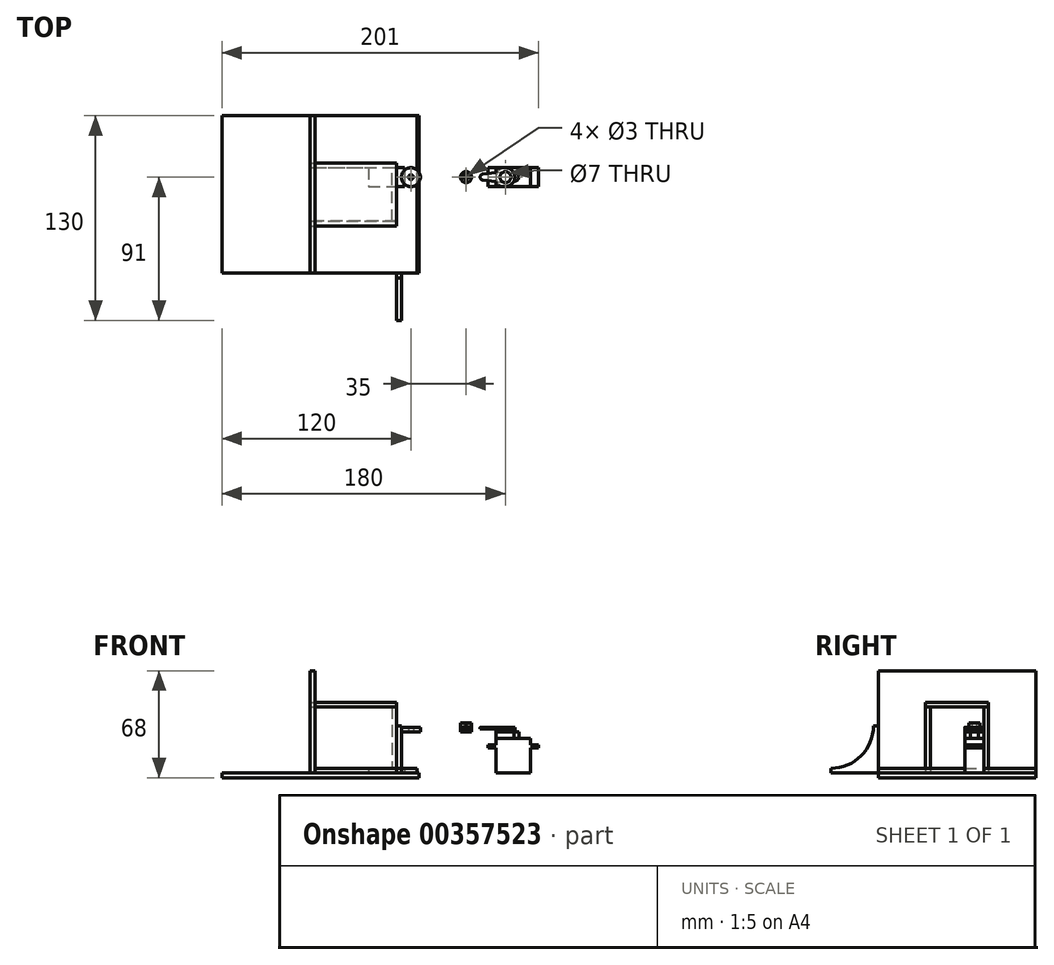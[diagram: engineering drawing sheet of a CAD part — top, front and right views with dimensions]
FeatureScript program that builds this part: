
annotation { "Feature Type Name" : "Feature", "Feature Type Description" : "" }
export const myFeature = defineFeature(function(context is Context, id is Id, definition is map)
    precondition{}
    {
        {
            var Q0;
            Q0=qCreatedBy(makeId("Front.planeOp"),FACE);
            var sketch = newSketch(context, id + "F0", { "sketchPlane" : qUnion([Q0])});
            skLineSegment(sketch, "E0", {"start": v(0, 0) * mm, "end": v(22, 0) * mm});
            skLineSegment(sketch, "E1", {"start": v(22, 0) * mm, "end": v(22, 16) * mm});
            skLineSegment(sketch, "E2", {"start": v(22, 16) * mm, "end": v(27, 16) * mm});
            skLineSegment(sketch, "E3", {"start": v(27, 16) * mm, "end": v(27, 18) * mm});
            skLineSegment(sketch, "E4", {"start": v(27, 18) * mm, "end": v(22, 18) * mm});
            skLineSegment(sketch, "E5", {"start": v(22, 18) * mm, "end": v(22, 22) * mm});
            skLineSegment(sketch, "E6", {"start": v(22, 22) * mm, "end": v(0, 22) * mm});
            skLineSegment(sketch, "E7", {"start": v(0, 22) * mm, "end": v(0, 18) * mm});
            skLineSegment(sketch, "E8", {"start": v(0, 18) * mm, "end": v(-5, 18) * mm});
            skLineSegment(sketch, "E9", {"start": v(-5, 18) * mm, "end": v(-5, 16) * mm});
            skLineSegment(sketch, "E10", {"start": v(-5, 16) * mm, "end": v(0, 16) * mm});
            skLineSegment(sketch, "E11", {"start": v(0, 16) * mm, "end": v(0, 0) * mm});
            skSolve(sketch);
        }
        {
            var Q0;
            Q0=makeQuery(id+"F0.imprint","IMPRINT",FACE,{"disambiguationData":[TD([[makeQuery(id+"F0.imprint","IMPRINT",EDGE,{"derivedFrom":sQuery(id+"F0.wireOp",EDGE,"E0")}),1.0]])]});
            extrude(context, id + "F1", {"entities" : qUnion([Q0]), "oppositeDirection" : true, "depth" : 17 * mm, "hasSecondDirection" : true, "secondDirectionOppositeDirection" : true, "secondDirectionDepth" : 5 * mm});
        }
        {
            var Q0;
            Q0=qCreatedBy(makeId("Right.planeOp"),FACE);
            cPlane(context, id + "F2", {"entities" : qUnion([Q0]), "cplaneType" : CPlaneType.OFFSET, "offset" : 63 * mm, "oppositeDirection" : true, "width" : 150 * mm, "height" : 150 * mm});
        }
        {
            var Q0;
            Q0=makeQuery(id+"F1.opExtrude","SWEPT_FACE",FACE,{"disambiguationData":[OSD([sQuery(id+"F0.wireOp",EDGE,"E6")])]});
            var sketch = newSketch(context, id + "F3", { "sketchPlane" : qUnion([Q0])});
            skCircle(sketch, "E12", {"center": v(6, 11) * mm, "radius": 6 * mm});
            skCircle(sketch, "E13", {"center": v(12, 11) * mm, "radius": 2.5 * mm});
            skCircle(sketch, "E14", {"center": v(-19, 11) * mm, "radius": 3.5 * mm});
            skLineSegment(sketch, "E15", {"start": v(-19.35, 7.52) * mm, "end": v(5.4, 5.03) * mm});
            skLineSegment(sketch, "E16", {"start": v(-19.35, 14.48) * mm, "end": v(5.4, 16.97) * mm});
            skCircle(sketch, "E17", {"center": v(-54, 11) * mm, "radius": 6 * mm});
            skLineSegment(sketch, "E18", {"start": v(-54, 5) * mm, "end": v(-63, 5) * mm});
            skLineSegment(sketch, "E19", {"start": v(-63, 17) * mm, "end": v(-54, 17) * mm});
            skLineSegment(sketch, "E20", {"start": v(6, 11) * mm, "end": v(12, 11) * mm, "construction": true});
            skLineSegment(sketch, "E21", {"start": v(6, 11) * mm, "end": v(-19, 11) * mm, "construction": true});
            skLineSegment(sketch, "E22", {"start": v(-19, 11) * mm, "end": v(-54, 11) * mm, "construction": true});
            skLineSegment(sketch, "E23", {"start": v(-53.57, 16.98) * mm, "end": v(-18.75, 14.5) * mm});
            skLineSegment(sketch, "E24", {"start": v(-53.57, 5.02) * mm, "end": v(-18.75, 7.5) * mm});
            skCircle(sketch, "E25", {"center": v(-54, 11) * mm, "radius": 1.5 * mm});
            skCircle(sketch, "E26", {"center": v(-19, 11) * mm, "radius": 1.5 * mm});
            skCircle(sketch, "E27", {"center": v(6, 11) * mm, "radius": 3.5 * mm});
            skCircle(sketch, "E28", {"center": v(-8, 11) * mm, "radius": 2 * mm});
            skLineSegment(sketch, "E29", {"start": v(-8.21, 9.01) * mm, "end": v(5.62, 7.52) * mm});
            skLineSegment(sketch, "E30", {"start": v(-8.21, 12.99) * mm, "end": v(5.63, 14.48) * mm});
            skLineSegment(sketch, "E31", {"start": v(-63, 17) * mm, "end": v(-63, 14) * mm});
            skLineSegment(sketch, "E32", {"start": v(-63, 14) * mm, "end": v(-66, 14) * mm});
            skLineSegment(sketch, "E33", {"start": v(-66, 14) * mm, "end": v(-66, 8) * mm});
            skLineSegment(sketch, "E34", {"start": v(-66, 8) * mm, "end": v(-63, 8) * mm});
            skLineSegment(sketch, "E35", {"start": v(-63, 8) * mm, "end": v(-63, 5) * mm});
            skSolve(sketch);
        }
        {
            var Q0;
            {var subQ0=sQuery(id+"F3.wireOp",EDGE,"E12");var subQ1=sQuery(id+"F0.wireOp",EDGE,"E6");var subQ3=makeQuery(id+"F3.imprint","INTERSECT",VERTEX,{"derivedFrom":[makeQuery(id+"F1.opExtrude","CAP_EDGE",EDGE,{"disambiguationData":[OSD([subQ1])],"isStart":true}),subQ0]});Q0=makeQuery(id+"F3.imprint","IMPRINT",FACE,{"disambiguationData":[TD([[makeQuery(id+"F3.imprint","IMPRINT",EDGE,{"disambiguationData":[TD([[subQ3,1.0]])],"derivedFrom":subQ0}),1.0]])]});}
            var Q1;
            {var subQ0=sQuery(id+"F3.wireOp",EDGE,"E13");var subQ1=sQuery(id+"F3.wireOp",EDGE,"E12");var subQ2=makeQuery(id+"F3.imprint","INTERSECT",VERTEX,{"disambiguationData":[OD(0.0)],"derivedFrom":[subQ1,subQ0]});Q1=makeQuery(id+"F3.imprint","IMPRINT",FACE,{"disambiguationData":[TD([[makeQuery(id+"F3.imprint","IMPRINT",EDGE,{"disambiguationData":[TD([[subQ2,1.0]])],"derivedFrom":subQ1}),1.0]])]});}
            var Q2;
            {var subQ0=sQuery(id+"F3.wireOp",EDGE,"E13");var subQ1=sQuery(id+"F3.wireOp",EDGE,"E12");var subQ2=makeQuery(id+"F3.imprint","INTERSECT",VERTEX,{"disambiguationData":[OD(0.0)],"derivedFrom":[subQ1,subQ0]});Q2=makeQuery(id+"F3.imprint","IMPRINT",FACE,{"disambiguationData":[TD([[makeQuery(id+"F3.imprint","IMPRINT",EDGE,{"disambiguationData":[TD([[subQ2,1.0]])],"derivedFrom":subQ1}),-1.0]])]});}
            var Q3;
            {var subQ0=sQuery(id+"F3.wireOp",EDGE,"E13");var subQ1=sQuery(id+"F3.wireOp",EDGE,"E12");var subQ2=makeQuery(id+"F3.imprint","INTERSECT",VERTEX,{"disambiguationData":[OD(0.0)],"derivedFrom":[subQ1,subQ0]});Q3=makeQuery(id+"F3.imprint","IMPRINT",FACE,{"disambiguationData":[TD([[makeQuery(id+"F3.imprint","IMPRINT",EDGE,{"disambiguationData":[TD([[subQ2,-1.0]])],"derivedFrom":subQ1}),1.0]])]});}
            var Q4;
            {var subQ0=sQuery(id+"F3.wireOp",EDGE,"E29");var subQ1=sQuery(id+"F3.wireOp",EDGE,"E27");var subQ2=makeQuery(id+"F3.imprint","INTERSECT",VERTEX,{"derivedFrom":[subQ1,subQ0]});Q4=makeQuery(id+"F3.imprint","IMPRINT",FACE,{"disambiguationData":[TD([[makeQuery(id+"F3.imprint","IMPRINT",EDGE,{"disambiguationData":[TD([[subQ2,1.0]])],"derivedFrom":subQ1}),-1.0]])]});}
            var Q5;
            {var subQ0=sQuery(id+"F3.wireOp",EDGE,"E27");var subQ1=makeQuery(id+"F3.imprint","INTERSECT",VERTEX,{"derivedFrom":[subQ0,sQuery(id+"F3.wireOp",EDGE,"E30")]});Q5=makeQuery(id+"F3.imprint","IMPRINT",FACE,{"disambiguationData":[TD([[makeQuery(id+"F3.imprint","IMPRINT",EDGE,{"disambiguationData":[TD([[subQ1,1.0]])],"derivedFrom":subQ0}),1.0]])]});}
            extrude(context, id + "F4", {"entities" : qUnion([Q0, Q1, Q2, Q3, Q4, Q5]), "operationType" : NewBodyOperationType.ADD, "depth" : 4 * mm});
        }
        {
            var Q0;
            {var subQ0=sQuery(id+"F3.wireOp",EDGE,"E15");var subQ1=sQuery(id+"F3.wireOp",EDGE,"E12");var subQ2=makeQuery(id+"F3.imprint","INTERSECT",VERTEX,{"derivedFrom":[subQ1,subQ0]});Q0=makeQuery(id+"F3.imprint","IMPRINT",FACE,{"disambiguationData":[TD([[makeQuery(id+"F3.imprint","IMPRINT",EDGE,{"disambiguationData":[TD([[subQ2,1.0]])],"derivedFrom":subQ1}),-1.0]])]});}
            var Q1;
            Q1=makeQuery(id+"F3.imprint","IMPRINT",FACE,{"disambiguationData":[TD([[makeQuery(id+"F3.imprint","IMPRINT",EDGE,{"derivedFrom":sQuery(id+"F3.wireOp",EDGE,"E26")}),-1.0]])]});
            var Q2;
            {var subQ0=sQuery(id+"F3.wireOp",EDGE,"E13");var subQ1=sQuery(id+"F3.wireOp",EDGE,"E12");var subQ2=makeQuery(id+"F3.imprint","INTERSECT",VERTEX,{"disambiguationData":[OD(0.0)],"derivedFrom":[subQ1,subQ0]});Q2=makeQuery(id+"F3.imprint","IMPRINT",FACE,{"disambiguationData":[TD([[makeQuery(id+"F3.imprint","IMPRINT",EDGE,{"disambiguationData":[TD([[subQ2,-1.0]])],"derivedFrom":subQ1}),1.0]])]});}
            var Q3;
            {var subQ0=sQuery(id+"F3.wireOp",EDGE,"E13");var subQ1=sQuery(id+"F3.wireOp",EDGE,"E12");var subQ2=makeQuery(id+"F3.imprint","INTERSECT",VERTEX,{"disambiguationData":[OD(0.0)],"derivedFrom":[subQ1,subQ0]});Q3=makeQuery(id+"F3.imprint","IMPRINT",FACE,{"disambiguationData":[TD([[makeQuery(id+"F3.imprint","IMPRINT",EDGE,{"disambiguationData":[TD([[subQ2,1.0]])],"derivedFrom":subQ1}),1.0]])]});}
            var Q4;
            {var subQ0=sQuery(id+"F3.wireOp",EDGE,"E16");var subQ1=sQuery(id+"F3.wireOp",EDGE,"E12");var subQ2=makeQuery(id+"F3.imprint","INTERSECT",VERTEX,{"derivedFrom":[subQ1,subQ0]});Q4=makeQuery(id+"F3.imprint","IMPRINT",FACE,{"disambiguationData":[TD([[makeQuery(id+"F3.imprint","IMPRINT",EDGE,{"disambiguationData":[TD([[subQ2,-1.0]])],"derivedFrom":subQ1}),-1.0]])]});}
            var Q5;
            {var subQ5=sQuery(id+"F3.wireOp",EDGE,"E23");var subQ6=sQuery(id+"F3.wireOp",EDGE,"E14");var subQ7=makeQuery(id+"F3.imprint","INTERSECT",VERTEX,{"derivedFrom":[subQ6,subQ5]});Q5=makeQuery(id+"F3.imprint","IMPRINT",FACE,{"disambiguationData":[TD([[makeQuery(id+"F3.imprint","IMPRINT",EDGE,{"disambiguationData":[TD([[subQ7,-1.0]])],"derivedFrom":subQ6}),1.0]])]});}
            var Q6;
            {var subQ1=sQuery(id+"F3.wireOp",EDGE,"E12");var subQ4=makeQuery(id+"F3.imprint","INTERSECT",VERTEX,{"derivedFrom":[subQ1,sQuery(id+"F3.wireOp",EDGE,"E15")]});Q6=makeQuery(id+"F3.imprint","IMPRINT",FACE,{"disambiguationData":[TD([[makeQuery(id+"F3.imprint","IMPRINT",EDGE,{"disambiguationData":[TD([[subQ4,1.0]])],"derivedFrom":subQ1}),1.0]])]});}
            var Q7;
            {var subQ0=sQuery(id+"F3.wireOp",EDGE,"E16");var subQ1=sQuery(id+"F3.wireOp",EDGE,"E14");var subQ2=makeQuery(id+"F3.imprint","INTERSECT",VERTEX,{"derivedFrom":[subQ1,subQ0]});Q7=makeQuery(id+"F3.imprint","IMPRINT",FACE,{"disambiguationData":[TD([[makeQuery(id+"F3.imprint","IMPRINT",EDGE,{"disambiguationData":[TD([[subQ2,-1.0]])],"derivedFrom":subQ1}),1.0]])]});}
            var Q8;
            {var subQ0=sQuery(id+"F3.wireOp",EDGE,"E15");var subQ1=sQuery(id+"F3.wireOp",EDGE,"E14");var subQ2=makeQuery(id+"F3.imprint","INTERSECT",VERTEX,{"derivedFrom":[subQ1,subQ0]});Q8=makeQuery(id+"F3.imprint","IMPRINT",FACE,{"disambiguationData":[TD([[makeQuery(id+"F3.imprint","IMPRINT",EDGE,{"disambiguationData":[TD([[subQ2,1.0]])],"derivedFrom":subQ1}),1.0]])]});}
            extrude(context, id + "F5", {"entities" : qUnion([Q0, Q1, Q2, Q3, Q4, Q5, Q6, Q7, Q8]), "depth" : 6 * mm, "hasSecondDirection" : true, "secondDirectionOppositeDirection" : false, "secondDirectionDepth" : 4 * mm});
        }
        {
            var Q0;
            Q0=makeQuery(id+"F3.imprint","IMPRINT",FACE,{"disambiguationData":[TD([[makeQuery(id+"F3.imprint","IMPRINT",EDGE,{"derivedFrom":sQuery(id+"F3.wireOp",EDGE,"E26")}),-1.0]])]});
            var Q1;
            {var subQ5=sQuery(id+"F3.wireOp",EDGE,"E23");var subQ6=sQuery(id+"F3.wireOp",EDGE,"E14");var subQ7=makeQuery(id+"F3.imprint","INTERSECT",VERTEX,{"derivedFrom":[subQ6,subQ5]});Q1=makeQuery(id+"F3.imprint","IMPRINT",FACE,{"disambiguationData":[TD([[makeQuery(id+"F3.imprint","IMPRINT",EDGE,{"disambiguationData":[TD([[subQ7,-1.0]])],"derivedFrom":subQ6}),1.0]])]});}
            var Q2;
            {var subQ0=sQuery(id+"F3.wireOp",EDGE,"E28");var subQ1=makeQuery(id+"F3.imprint","INTERSECT",VERTEX,{"derivedFrom":[subQ0,sQuery(id+"F3.wireOp",EDGE,"E29")]});Q2=makeQuery(id+"F3.imprint","IMPRINT",FACE,{"disambiguationData":[TD([[makeQuery(id+"F3.imprint","IMPRINT",EDGE,{"disambiguationData":[TD([[subQ1,1.0]])],"derivedFrom":subQ0}),1.0]])]});}
            var Q3;
            {var subQ1=sQuery(id+"F3.wireOp",EDGE,"E28");var subQ6=sQuery(id+"F3.wireOp",EDGE,"E29");var subQ8=makeQuery(id+"F3.imprint","INTERSECT",VERTEX,{"derivedFrom":[subQ1,subQ6]});Q3=makeQuery(id+"F3.imprint","IMPRINT",FACE,{"disambiguationData":[TD([[makeQuery(id+"F3.imprint","IMPRINT",EDGE,{"disambiguationData":[TD([[subQ8,-1.0]])],"derivedFrom":subQ1}),-1.0]])]});}
            var Q4;
            {var subQ0=sQuery(id+"F3.wireOp",EDGE,"E16");var subQ1=sQuery(id+"F3.wireOp",EDGE,"E12");var subQ2=makeQuery(id+"F3.imprint","INTERSECT",VERTEX,{"derivedFrom":[subQ1,subQ0]});Q4=makeQuery(id+"F3.imprint","IMPRINT",FACE,{"disambiguationData":[TD([[makeQuery(id+"F3.imprint","IMPRINT",EDGE,{"disambiguationData":[TD([[subQ2,-1.0]])],"derivedFrom":subQ1}),-1.0]])]});}
            var Q5;
            {var subQ0=sQuery(id+"F3.wireOp",EDGE,"E30");var subQ1=sQuery(id+"F3.wireOp",EDGE,"E12");var subQ2=makeQuery(id+"F3.imprint","INTERSECT",VERTEX,{"derivedFrom":[subQ1,subQ0]});Q5=makeQuery(id+"F3.imprint","IMPRINT",FACE,{"disambiguationData":[TD([[makeQuery(id+"F3.imprint","IMPRINT",EDGE,{"disambiguationData":[TD([[subQ2,-1.0]])],"derivedFrom":subQ1}),-1.0]])]});}
            var Q6;
            {var subQ0=sQuery(id+"F3.wireOp",EDGE,"E29");var subQ1=sQuery(id+"F3.wireOp",EDGE,"E12");var subQ2=makeQuery(id+"F3.imprint","INTERSECT",VERTEX,{"derivedFrom":[subQ1,subQ0]});Q6=makeQuery(id+"F3.imprint","IMPRINT",FACE,{"disambiguationData":[TD([[makeQuery(id+"F3.imprint","IMPRINT",EDGE,{"disambiguationData":[TD([[subQ2,1.0]])],"derivedFrom":subQ1}),-1.0]])]});}
            var Q7;
            {var subQ0=sQuery(id+"F3.wireOp",EDGE,"E15");var subQ1=sQuery(id+"F3.wireOp",EDGE,"E12");var subQ2=makeQuery(id+"F3.imprint","INTERSECT",VERTEX,{"derivedFrom":[subQ1,subQ0]});Q7=makeQuery(id+"F3.imprint","IMPRINT",FACE,{"disambiguationData":[TD([[makeQuery(id+"F3.imprint","IMPRINT",EDGE,{"disambiguationData":[TD([[subQ2,1.0]])],"derivedFrom":subQ1}),-1.0]])]});}
            var Q8;
            {var subQ0=sQuery(id+"F3.wireOp",EDGE,"E29");var subQ1=sQuery(id+"F3.wireOp",EDGE,"E27");var subQ2=makeQuery(id+"F3.imprint","INTERSECT",VERTEX,{"derivedFrom":[subQ1,subQ0]});Q8=makeQuery(id+"F3.imprint","IMPRINT",FACE,{"disambiguationData":[TD([[makeQuery(id+"F3.imprint","IMPRINT",EDGE,{"disambiguationData":[TD([[subQ2,1.0]])],"derivedFrom":subQ1}),-1.0]])]});}
            var Q9;
            {var subQ0=sQuery(id+"F3.wireOp",EDGE,"E13");var subQ1=sQuery(id+"F3.wireOp",EDGE,"E12");var subQ2=makeQuery(id+"F3.imprint","INTERSECT",VERTEX,{"disambiguationData":[OD(0.0)],"derivedFrom":[subQ1,subQ0]});Q9=makeQuery(id+"F3.imprint","IMPRINT",FACE,{"disambiguationData":[TD([[makeQuery(id+"F3.imprint","IMPRINT",EDGE,{"disambiguationData":[TD([[subQ2,-1.0]])],"derivedFrom":subQ1}),1.0]])]});}
            var Q10;
            {var subQ1=sQuery(id+"F3.wireOp",EDGE,"E12");var subQ4=makeQuery(id+"F3.imprint","INTERSECT",VERTEX,{"derivedFrom":[subQ1,sQuery(id+"F3.wireOp",EDGE,"E15")]});Q10=makeQuery(id+"F3.imprint","IMPRINT",FACE,{"disambiguationData":[TD([[makeQuery(id+"F3.imprint","IMPRINT",EDGE,{"disambiguationData":[TD([[subQ4,1.0]])],"derivedFrom":subQ1}),1.0]])]});}
            var Q11;
            {var subQ0=sQuery(id+"F3.wireOp",EDGE,"E13");var subQ1=sQuery(id+"F3.wireOp",EDGE,"E12");var subQ2=makeQuery(id+"F3.imprint","INTERSECT",VERTEX,{"disambiguationData":[OD(0.0)],"derivedFrom":[subQ1,subQ0]});Q11=makeQuery(id+"F3.imprint","IMPRINT",FACE,{"disambiguationData":[TD([[makeQuery(id+"F3.imprint","IMPRINT",EDGE,{"disambiguationData":[TD([[subQ2,1.0]])],"derivedFrom":subQ1}),1.0]])]});}
            var Q12;
            {var subQ0=sQuery(id+"F3.wireOp",EDGE,"E15");var subQ1=sQuery(id+"F3.wireOp",EDGE,"E14");var subQ2=makeQuery(id+"F3.imprint","INTERSECT",VERTEX,{"derivedFrom":[subQ1,subQ0]});Q12=makeQuery(id+"F3.imprint","IMPRINT",FACE,{"disambiguationData":[TD([[makeQuery(id+"F3.imprint","IMPRINT",EDGE,{"disambiguationData":[TD([[subQ2,1.0]])],"derivedFrom":subQ1}),1.0]])]});}
            var Q13;
            {var subQ0=sQuery(id+"F3.wireOp",EDGE,"E16");var subQ1=sQuery(id+"F3.wireOp",EDGE,"E14");var subQ2=makeQuery(id+"F3.imprint","INTERSECT",VERTEX,{"derivedFrom":[subQ1,subQ0]});Q13=makeQuery(id+"F3.imprint","IMPRINT",FACE,{"disambiguationData":[TD([[makeQuery(id+"F3.imprint","IMPRINT",EDGE,{"disambiguationData":[TD([[subQ2,-1.0]])],"derivedFrom":subQ1}),1.0]])]});}
            extrude(context, id + "F6", {"entities" : qUnion([Q0, Q1, Q2, Q3, Q4, Q5, Q6, Q7, Q8, Q9, Q10, Q11, Q12, Q13]), "depth" : 7 * mm, "hasSecondDirection" : true, "secondDirectionOppositeDirection" : false, "secondDirectionDepth" : 6 * mm});
        }
        {
            var Q0;
            {var subQ0=sQuery(id+"F3.wireOp",EDGE,"E14");var subQ1=makeQuery(id+"F3.imprint","INTERSECT",VERTEX,{"derivedFrom":[subQ0,sQuery(id+"F3.wireOp",EDGE,"E15"),sQuery(id+"F3.wireOp",EDGE,"TpgKvrXl-maDU-2S3D-b7ML-qU1TAJrhzgWD")]});Q0=makeQuery(id+"F3.imprint","IMPRINT",FACE,{"disambiguationData":[TD([[makeQuery(id+"F3.imprint","IMPRINT",EDGE,{"disambiguationData":[TD([[subQ1,-1.0]])],"derivedFrom":subQ0}),1.0]])]});}
            var Q1;
            {var subQ0=sQuery(id+"F3.wireOp",EDGE,"E17");var subQ1=makeQuery(id+"F3.imprint","INTERSECT",VERTEX,{"derivedFrom":[sQuery(id+"F3.wireOp",EDGE,"TpgKvrXl-maDU-2S3D-b7ML-qU1TAJrhzgWD"),subQ0,sQuery(id+"F3.wireOp",EDGE,"E18")]});Q1=makeQuery(id+"F3.imprint","IMPRINT",FACE,{"disambiguationData":[TD([[makeQuery(id+"F3.imprint","IMPRINT",EDGE,{"disambiguationData":[TD([[subQ1,-1.0]])],"derivedFrom":subQ0}),-1.0]])]});}
            var Q2;
            {var subQ0=sQuery(id+"F3.wireOp",EDGE,"E14");var subQ1=makeQuery(id+"F3.imprint","INTERSECT",VERTEX,{"derivedFrom":[subQ0,sQuery(id+"F3.wireOp",EDGE,"E15"),sQuery(id+"F3.wireOp",EDGE,"TpgKvrXl-maDU-2S3D-b7ML-qU1TAJrhzgWD")]});Q2=makeQuery(id+"F3.imprint","IMPRINT",FACE,{"disambiguationData":[TD([[makeQuery(id+"F3.imprint","IMPRINT",EDGE,{"disambiguationData":[TD([[subQ1,-1.0]])],"derivedFrom":subQ0}),-1.0]])]});}
            var Q3;
            {var subQ0=sQuery(id+"F3.wireOp",EDGE,"E15");var subQ1=sQuery(id+"F3.wireOp",EDGE,"E14");var subQ2=makeQuery(id+"F3.imprint","INTERSECT",VERTEX,{"derivedFrom":[subQ1,subQ0]});Q3=makeQuery(id+"F3.imprint","IMPRINT",FACE,{"disambiguationData":[TD([[makeQuery(id+"F3.imprint","IMPRINT",EDGE,{"disambiguationData":[TD([[subQ2,1.0]])],"derivedFrom":subQ1}),1.0]])]});}
            var Q4;
            {var subQ0=sQuery(id+"F3.wireOp",EDGE,"E16");var subQ1=sQuery(id+"F3.wireOp",EDGE,"E14");var subQ2=makeQuery(id+"F3.imprint","INTERSECT",VERTEX,{"derivedFrom":[subQ1,subQ0]});Q4=makeQuery(id+"F3.imprint","IMPRINT",FACE,{"disambiguationData":[TD([[makeQuery(id+"F3.imprint","IMPRINT",EDGE,{"disambiguationData":[TD([[subQ2,-1.0]])],"derivedFrom":subQ1}),1.0]])]});}
            extrude(context, id + "F7", {"entities" : qUnion([Q0, Q1, Q2, Q3, Q4]), "depth" : 10 * mm, "hasSecondDirection" : true, "secondDirectionOppositeDirection" : false, "secondDirectionDepth" : 7 * mm});
        }
        {
            var Q0;
            Q0=qCreatedBy(id+"F2.planeOp",FACE);
            var sketch = newSketch(context, id + "F8", { "sketchPlane" : qUnion([Q0])});
            skLineSegment(sketch, "E36.bottom", {"start": v(-20, 0) * mm, "end": v(20, 0) * mm});
            skLineSegment(sketch, "E36.top", {"start": v(-20, 45) * mm, "end": v(20, 45) * mm});
            skLineSegment(sketch, "E36.left", {"start": v(-20, 0) * mm, "end": v(-20, 45) * mm});
            skLineSegment(sketch, "E36.right", {"start": v(20, 0) * mm, "end": v(20, 45) * mm});
            skLineSegment(sketch, "E37", {"start": v(-20, 42) * mm, "end": v(20, 42) * mm});
            skLineSegment(sketch, "E38", {"start": v(-17, 42) * mm, "end": v(-17, 0) * mm});
            skLineSegment(sketch, "E39", {"start": v(17, 42) * mm, "end": v(17, 0) * mm});
            skLineSegment(sketch, "E40", {"start": v(-20, 0) * mm, "end": v(-50, 0) * mm});
            skLineSegment(sketch, "E41", {"start": v(-50, 0) * mm, "end": v(-50, 65) * mm});
            skLineSegment(sketch, "E42", {"start": v(-50, 65) * mm, "end": v(50, 65) * mm});
            skLineSegment(sketch, "E43", {"start": v(50, 65) * mm, "end": v(50, 0) * mm});
            skLineSegment(sketch, "E44", {"start": v(50, 0) * mm, "end": v(20, 0) * mm});
            skLineSegment(sketch, "E45", {"start": v(-50, 0) * mm, "end": v(-50, -3) * mm});
            skLineSegment(sketch, "E46", {"start": v(-50, -3) * mm, "end": v(50, -3) * mm});
            skLineSegment(sketch, "E47", {"start": v(50, -3) * mm, "end": v(50, 0) * mm});
            skLineSegment(sketch, "E48", {"start": v(-17, 3) * mm, "end": v(17, 3) * mm});
            skLineSegment(sketch, "E49", {"start": v(-50, 0) * mm, "end": v(-80, 0) * mm});
            skLineSegment(sketch, "E50", {"start": v(-80, 0) * mm, "end": v(-80, 3) * mm});
            skLineSegment(sketch, "E51", {"start": v(-53, 30) * mm, "end": v(-50, 30) * mm});
            skLineSegment(sketch, "E52", {"start": v(-50, 30) * mm, "end": v(-50, 0) * mm});
            skArc(sketch, "E53", {"start": v(-80, 3) * mm, "mid": v(-60.9, 10.9) * mm, "end": v(-53, 30) * mm});
            skSolve(sketch);
        }
        {
            var Q0;
            {var subQ3=sQuery(id+"F8.wireOp",EDGE,"E38");Q0=makeQuery(id+"F8.imprint","IMPRINT",FACE,{"disambiguationData":[TD([[makeQuery(id+"F8.imprint","IMPRINT",EDGE,{"derivedFrom":subQ3}),-1.0]])]});}
            extrude(context, id + "F9", {"entities" : qUnion([Q0]), "oppositeDirection" : true, "depth" : 55 * mm});
        }
        {
            var Q0;
            {var subQ3=sQuery(id+"F8.wireOp",EDGE,"E39");Q0=makeQuery(id+"F8.imprint","IMPRINT",FACE,{"disambiguationData":[TD([[makeQuery(id+"F8.imprint","IMPRINT",EDGE,{"derivedFrom":subQ3}),1.0]])]});}
            extrude(context, id + "F10", {"entities" : qUnion([Q0]), "oppositeDirection" : true, "depth" : 55 * mm});
        }
        {
            var Q0;
            {var subQ1=sQuery(id+"F8.wireOp",EDGE,"E36.top");Q0=makeQuery(id+"F8.imprint","IMPRINT",FACE,{"disambiguationData":[TD([[makeQuery(id+"F8.imprint","IMPRINT",EDGE,{"derivedFrom":subQ1}),-1.0]])]});}
            extrude(context, id + "F11", {"entities" : qUnion([Q0]), "oppositeDirection" : true, "depth" : 55 * mm});
        }
        {
            var Q0;
            {var subQ5=sQuery(id+"F8.wireOp",EDGE,"E48");Q0=makeQuery(id+"F8.imprint","IMPRINT",FACE,{"disambiguationData":[TD([[makeQuery(id+"F8.imprint","IMPRINT",EDGE,{"derivedFrom":subQ5}),1.0]])]});}
            extrude(context, id + "F12", {"entities" : qUnion([Q0]), "oppositeDirection" : true, "depth" : 3 * mm});
        }
        {
            var Q0;
            {var subQ0=sQuery(id+"F8.wireOp",EDGE,"E38");Q0=makeQuery(id+"F8.imprint","IMPRINT",FACE,{"disambiguationData":[TD([[makeQuery(id+"F8.imprint","IMPRINT",EDGE,{"derivedFrom":subQ0}),1.0]])]});}
            extrude(context, id + "F13", {"entities" : qUnion([Q0]), "oppositeDirection" : true, "depth" : 55 * mm, "hasSecondDirection" : true, "secondDirectionOppositeDirection" : true, "secondDirectionDepth" : 52 * mm});
        }
        {
            var Q0;
            {var subQ0=sQuery(id+"F3.wireOp",EDGE,"E17");var subQ1=makeQuery(id+"F3.imprint","INTERSECT",VERTEX,{"derivedFrom":[sQuery(id+"F3.wireOp",EDGE,"TpgKvrXl-maDU-2S3D-b7ML-qU1TAJrhzgWD"),subQ0,sQuery(id+"F3.wireOp",EDGE,"E18")]});Q0=makeQuery(id+"F3.imprint","IMPRINT",FACE,{"disambiguationData":[TD([[makeQuery(id+"F3.imprint","IMPRINT",EDGE,{"disambiguationData":[TD([[subQ1,-1.0]])],"derivedFrom":subQ0}),1.0]])]});}
            var Q1;
            {var subQ0=sQuery(id+"F3.wireOp",EDGE,"E17");var subQ1=makeQuery(id+"F3.imprint","INTERSECT",VERTEX,{"derivedFrom":[sQuery(id+"F3.wireOp",EDGE,"TpgKvrXl-maDU-2S3D-b7ML-qU1TAJrhzgWD"),subQ0,sQuery(id+"F3.wireOp",EDGE,"E18")]});Q1=makeQuery(id+"F3.imprint","IMPRINT",FACE,{"disambiguationData":[TD([[makeQuery(id+"F3.imprint","IMPRINT",EDGE,{"disambiguationData":[TD([[subQ1,-1.0]])],"derivedFrom":subQ0}),-1.0]])]});}
            extrude(context, id + "F14", {"entities" : qUnion([Q0, Q1]), "depth" : 7 * mm, "hasSecondDirection" : true, "secondDirectionOppositeDirection" : false, "secondDirectionDepth" : 4 * mm});
        }
        {
            var Q0;
            {var subQ6=sQuery(id+"F8.wireOp",EDGE,"E36.top");Q0=makeQuery(id+"F8.imprint","IMPRINT",FACE,{"disambiguationData":[TD([[makeQuery(id+"F8.imprint","IMPRINT",EDGE,{"derivedFrom":subQ6}),1.0]])]});}
            extrude(context, id + "F15", {"entities" : qUnion([Q0]), "oppositeDirection" : true, "depth" : 55 * mm, "hasSecondDirection" : true, "secondDirectionOppositeDirection" : true, "secondDirectionDepth" : 52 * mm});
        }
        {
            var Q0;
            {var subQ0=sQuery(id+"F8.wireOp",EDGE,"E40");Q0=makeQuery(id+"F8.imprint","IMPRINT",FACE,{"disambiguationData":[TD([[makeQuery(id+"F8.imprint","IMPRINT",EDGE,{"derivedFrom":subQ0}),1.0]])]});}
            extrude(context, id + "F16", {"entities" : qUnion([Q0]), "depth" : 14 * mm, "hasSecondDirection" : true, "secondDirectionOppositeDirection" : true, "secondDirectionDepth" : 111 * mm});
        }
        {
            var Q0;
            Q0=makeQuery(id+"F16.opExtrude","SWEPT_FACE",FACE,{"disambiguationData":[OSD([sQuery(id+"F8.wireOp",EDGE,"E36.bottom"),sQuery(id+"F8.wireOp",EDGE,"E40"),sQuery(id+"F8.wireOp",EDGE,"E44")])]});
            var sketch = newSketch(context, id + "F17", { "sketchPlane" : qUnion([Q0])});
            skLineSegment(sketch, "E54", {"start": v(-50, -50) * mm, "end": v(-50, 50) * mm});
            skLineSegment(sketch, "E55", {"start": v(-50, 50) * mm, "end": v(-115, 50) * mm});
            skLineSegment(sketch, "E56", {"start": v(-115, 50) * mm, "end": v(-115, 20) * mm});
            skLineSegment(sketch, "E57", {"start": v(-115, 20) * mm, "end": v(-63, 20) * mm});
            skLineSegment(sketch, "E58", {"start": v(-63, 20) * mm, "end": v(-63, 17) * mm});
            skLineSegment(sketch, "E59", {"start": v(-63, 17) * mm, "end": v(-58, 17) * mm});
            skLineSegment(sketch, "E60", {"start": v(-58, 17) * mm, "end": v(-58, 5) * mm});
            skLineSegment(sketch, "E61", {"start": v(-63.05, -20) * mm, "end": v(-115, -20) * mm});
            skLineSegment(sketch, "E62", {"start": v(-115, -20) * mm, "end": v(-115, -50) * mm});
            skLineSegment(sketch, "E63", {"start": v(-115, -50) * mm, "end": v(-50, -50) * mm});
            skLineSegment(sketch, "E64", {"start": v(-63.05, -20) * mm, "end": v(-63.05, -17) * mm});
            skLineSegment(sketch, "E65", {"start": v(-63.05, -17) * mm, "end": v(-114.97, -17) * mm});
            skLineSegment(sketch, "E66", {"start": v(-114.97, -17) * mm, "end": v(-114.97, 17) * mm});
            skLineSegment(sketch, "E67", {"start": v(-114.97, 17) * mm, "end": v(-81, 17) * mm});
            skLineSegment(sketch, "E68", {"start": v(-81, 17) * mm, "end": v(-81, 5) * mm});
            skLineSegment(sketch, "E69", {"start": v(-81, 5) * mm, "end": v(-58, 5) * mm});
            skSolve(sketch);
        }
        {
            var Q0;
            Q0=makeQuery(id+"F17.imprint","IMPRINT",FACE,{"disambiguationData":[TD([[makeQuery(id+"F17.imprint","IMPRINT",EDGE,{"derivedFrom":sQuery(id+"F17.wireOp",EDGE,"E54")}),1.0]])]});
            extrude(context, id + "F18", {"entities" : qUnion([Q0]), "depth" : 3 * mm});
        }
        {
            var Q0;
            Q0=makeQuery(id+"F14.opExtrude","SWEPT_BODY",BODY,{"disambiguationData":[OSD([sQuery(id+"F3.wireOp",EDGE,"E17"),sQuery(id+"F3.wireOp",EDGE,"E18"),sQuery(id+"F3.wireOp",EDGE,"XAJYiNmb-5G39-ey0C-2i26-8fCFaarhhL6o"),sQuery(id+"F3.wireOp",EDGE,"E19"),sQuery(id+"F3.wireOp",EDGE,"E25")])]});
            var Q1;
            Q1=makeQuery(id+"F12.opExtrude","SWEPT_BODY",BODY,{"disambiguationData":[OSD([sQuery(id+"F8.wireOp",EDGE,"E37"),sQuery(id+"F8.wireOp",EDGE,"E38"),sQuery(id+"F8.wireOp",EDGE,"E39"),sQuery(id+"F8.wireOp",EDGE,"E48")])]});
            booleanBodies(context, id + "F19", {"operationType" : BooleanOperationType.SUBTRACTION, "tools" : qUnion([Q0]), "targets" : qUnion([Q1]), "keepTools" : true});
        }
        {
            var Q0;
            Q0=makeQuery(id+"F8.imprint","IMPRINT",FACE,{"disambiguationData":[TD([[makeQuery(id+"F8.imprint","IMPRINT",EDGE,{"derivedFrom":sQuery(id+"F8.wireOp",EDGE,"E49")}),-1.0]])]});
            extrude(context, id + "F20", {"entities" : qUnion([Q0]), "depth" : 3 * mm});
        }
    });
